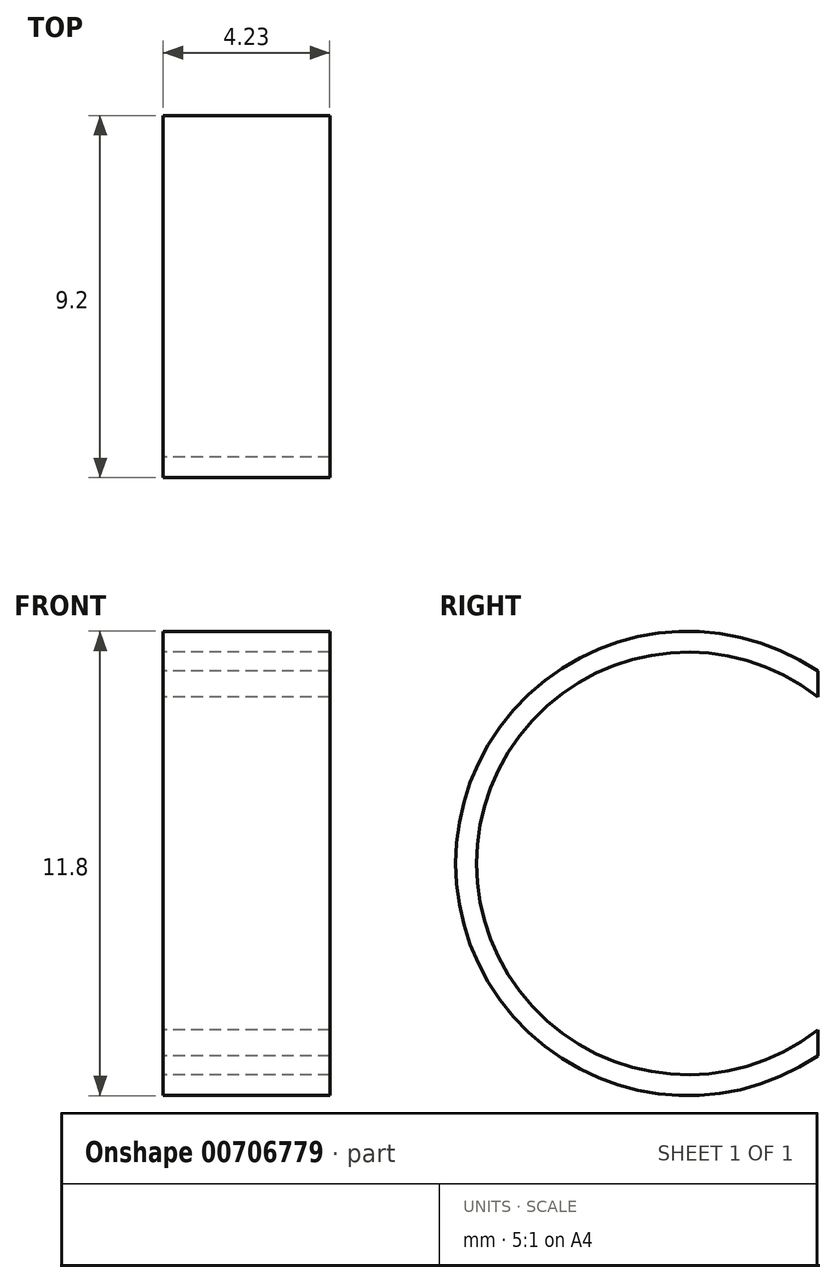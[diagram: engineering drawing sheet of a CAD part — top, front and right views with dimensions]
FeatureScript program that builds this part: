
annotation { "Feature Type Name" : "Feature", "Feature Type Description" : "" }
export const myFeature = defineFeature(function(context is Context, id is Id, definition is map)
    precondition{}
    {
        {
            var Q0;
            Q0=qCreatedBy(makeId("Right.planeOp"),FACE);
            var sketch = newSketch(context, id + "F0", { "sketchPlane" : qUnion([Q0])});
            skArc(sketch, "E0", {"start": v(0, 4.23) * mm, "mid": v(-8.67, 0) * mm, "end": v(0, -4.23) * mm});
            skArc(sketch, "E1", {"start": v(0, 4.89) * mm, "mid": v(-9.2, 0) * mm, "end": v(0, -4.89) * mm});
            skLineSegment(sketch, "E2", {"start": v(0, 4.89) * mm, "end": v(0, 4.23) * mm});
            skLineSegment(sketch, "E3", {"start": v(0, -4.23) * mm, "end": v(0, -4.89) * mm});
            skSolve(sketch);
        }
        {
            var Q0;
            Q0 = qSketchRegion(id + "F0", true);
            extrude(context, id + "F1", {"entities" : qUnion([Q0]), "depth" : 4.23 * mm, "offsetDistance" : 25.4 * mm});
        }
    });
